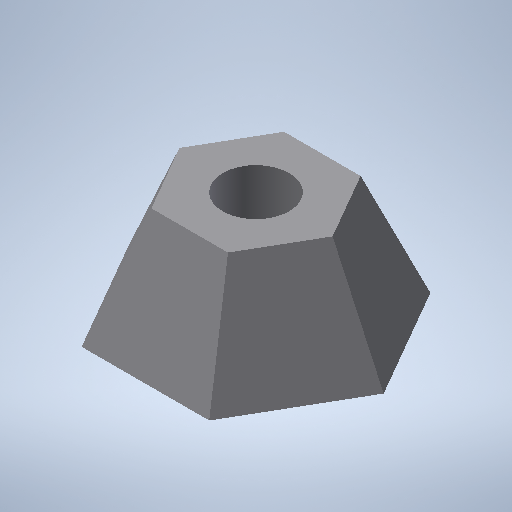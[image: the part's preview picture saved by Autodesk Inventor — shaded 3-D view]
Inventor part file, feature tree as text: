
AUTODESK INVENTOR PART (.ipt)
format: ipt  version: 2025 (Build 290162000, 162)  size: 238,592 bytes
history: native  units: mm (DEFAULTED — no unit token found)
features: sketch x2, plane x1, loft x1, hole x1
ambient origin geometry x8: Origin, YZ Plane, XZ Plane, XY Plane, X Axis, Y Axis, Z Axis, Center Point
bodies: Solid1 (feature_tree)
feature tree (5):
  sketch  "Sketch3"  dims[d16=0.0mm d17=90.0deg d18=0.0mm d19=90.0deg]
  plane  "Work Plane1"
  loft  "Loft1"
  hole  "Hole3"  [1 undecoded]
  sketch  "Sketch4"  dims[d29=6.0mm d30=4.0mm d31=2.0mm d32=14.3117mm d33=8.0mm d34=20.594885mm]
note: 1 required parameter value undecoded (feature->parameter linkage not recoverable at this tier; creation-order binding heuristic only, values carry confidence <= 0.55)
